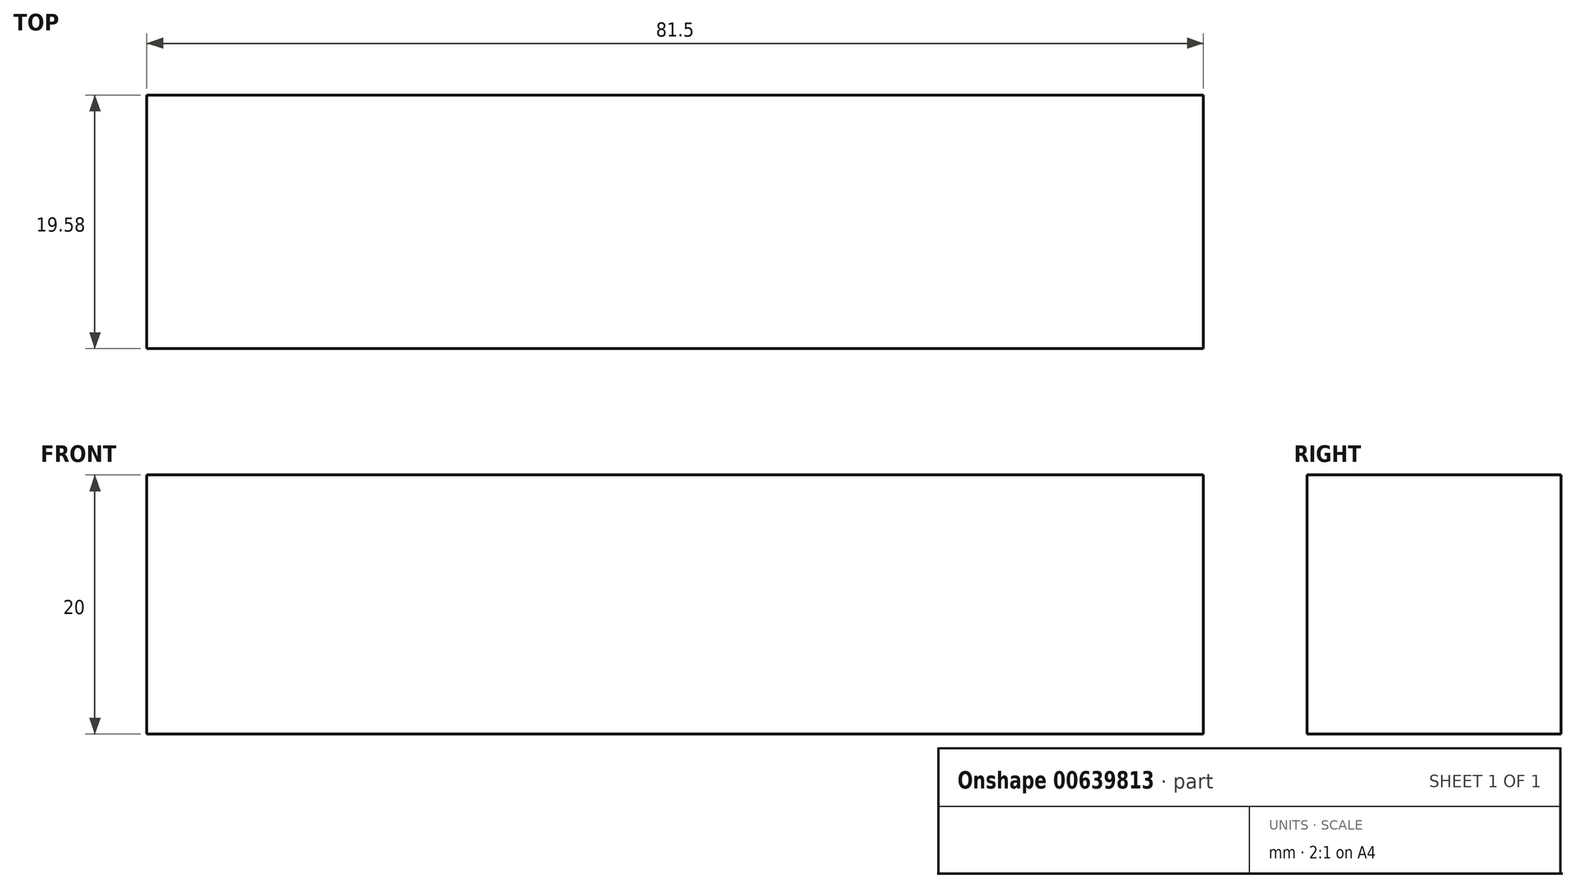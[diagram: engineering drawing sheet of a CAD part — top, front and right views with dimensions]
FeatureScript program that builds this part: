
annotation { "Feature Type Name" : "Feature", "Feature Type Description" : "" }
export const myFeature = defineFeature(function(context is Context, id is Id, definition is map)
    precondition{}
    {
        {
            var Q0;
            Q0=qCreatedBy(makeId("Top.planeOp"),FACE);
            var sketch = newSketch(context, id + "F0", { "sketchPlane" : qUnion([Q0])});
            skLineSegment(sketch, "E0.bottom", {"start": v(40.75, -9.79) * mm, "end": v(-40.75, -9.79) * mm});
            skLineSegment(sketch, "E0.top", {"start": v(40.75, 9.79) * mm, "end": v(-40.75, 9.79) * mm});
            skLineSegment(sketch, "E0.left", {"start": v(40.75, -9.79) * mm, "end": v(40.75, 9.79) * mm});
            skLineSegment(sketch, "E0.right", {"start": v(-40.75, -9.79) * mm, "end": v(-40.75, 9.79) * mm});
            skPoint(sketch, "E0.middle", {"position": v(0, 0) * mm});
            skSolve(sketch);
        }
        {
            var Q0;
            Q0=makeQuery(id+"F0.imprint","IMPRINT",FACE,{"disambiguationData":[TD([[makeQuery(id+"F0.imprint","IMPRINT",EDGE,{"derivedFrom":sQuery(id+"F0.wireOp",EDGE,"E0.bottom")}),-1.0]])]});
            extrude(context, id + "F1", {"entities" : qUnion([Q0]), "depth" : 20 * mm, "offsetDistance" : 25 * mm});
        }
    });
